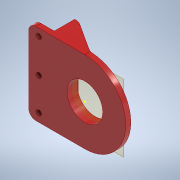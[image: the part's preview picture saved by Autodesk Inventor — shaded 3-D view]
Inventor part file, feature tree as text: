
AUTODESK INVENTOR PART (.ipt)
format: ipt  version: 2021.3 (Build 253353000, 353)  size: 269,312 bytes
history: native  units: mm
features: extrude x5, reference x5, sketch x3, fillet x3, other x3, plane x1, projected_geometry x1
ambient origin geometry x8: Origin, YZ Plane, XZ Plane, XY Plane, X Axis, Y Axis, Z Axis, Center Point
bodies: Solid1 (feature_tree)
feature tree (21):
  plane  "Work Plane1"
  extrude  "Extrusion1"  Depth=10.0mm
  sketch  "Sketch3"  dims[d1=10.0mm d2=5.0mm]
  extrude  "Extrusion2"  Depth=10.0mm
  extrude  "Extrusion3"  Depth=4.0mm
  extrude  "Extrusion4"  Depth=4.0mm
  fillet  "Fillet1"  Radius=20.0mm
  sketch  "Sketch6"  dims[d3=20.0mm d7=10.0mm]
  extrude  "Extrusion6"  TaperAngle=0.0deg  [1 undecoded]
  fillet  "Fillet2"  Radius=5.0mm
  fillet  "Fillet3"  Radius=5.0mm
  reference  "Reference1"
  reference  "Reference4"
  reference  "Reference6"
  reference  "Reference7"
  reference  "Reference8"
  projected_geometry  "Projected Loop1"
  sketch  "Sketch7"  dims[d8=5.0mm d9=0.0mm d10=20.0mm d11=4.0mm d12=20.0mm d15=0.0mm d16=0.0mm d17=5.0mm d18=0.0mm d19=5.0mm d20=0.0mm d21=10.0mm d22=10.0mm d23=5.0mm d24=5.0mm d25=5.0mm d29=7.0mm d30=7.0mm d31=35.0mm d32=4.0mm d33=10.0mm d34=0.0mm d35=13.962634mm d36=10.0mm d37=4.0mm d27=0.5mm d28=0.872665mm]
  other  "<userpath>\OneDrive - NXP\ROSinante\Mechanical\Frame Parts\motor assembly.iam"
  other  "motor assembly.iam"
  other  "Gearbox:1"
note: 1 required parameter value undecoded (feature->parameter linkage not recoverable at this tier; creation-order binding heuristic only, values carry confidence <= 0.55)
